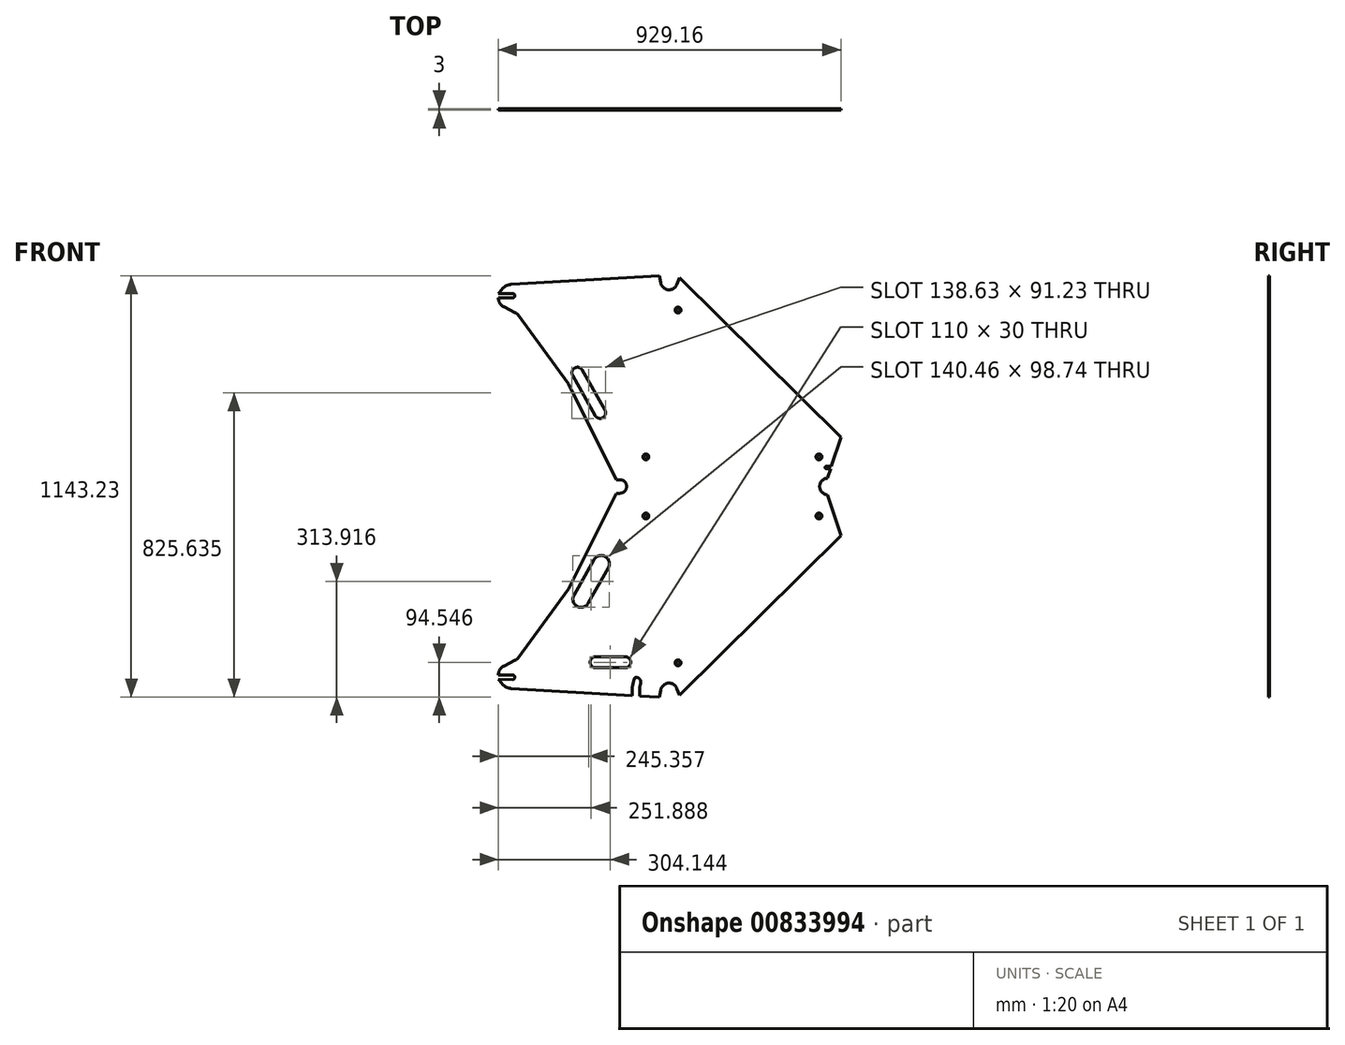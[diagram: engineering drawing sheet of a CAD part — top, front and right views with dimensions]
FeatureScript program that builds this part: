
annotation { "Feature Type Name" : "Feature", "Feature Type Description" : "" }
export const myFeature = defineFeature(function(context is Context, id is Id, definition is map)
    precondition{}
    {
        {
            var Q0;
            Q0=qCreatedBy(makeId("Front.planeOp"),FACE);
            var sketch = newSketch(context, id + "F0", { "sketchPlane" : qUnion([Q0])});
            skLineSegment(sketch, "E0", {"start": v(-160.76, 555.88) * mm, "end": v(408.24, 555.88) * mm, "construction": true});
            skLineSegment(sketch, "E1", {"start": v(408.24, 555.88) * mm, "end": v(445.83, 440.87) * mm, "construction": true});
            skArc(sketch, "E2", {"start": v(0.74, 26.27) * mm, "mid": v(-22.4, 40.64) * mm, "end": v(-42.43, 22.2) * mm});
            skLineSegment(sketch, "E3", {"start": v(-20.28, 18.24) * mm, "end": v(-144.86, 555.88) * mm, "construction": true});
            skLineSegment(sketch, "E4", {"start": v(-160.76, 555.88) * mm, "end": v(-39.05, 30.64) * mm, "construction": true});
            skLineSegment(sketch, "E5", {"start": v(-128.12, 555.88) * mm, "end": v(-7.89, 37.02) * mm, "construction": true});
            skLineSegment(sketch, "E6", {"start": v(0, 0) * mm, "end": v(-484.19, 28.1) * mm, "construction": true});
            skLineSegment(sketch, "E7", {"start": v(-160.76, 555.88) * mm, "end": v(-484.19, 28.1) * mm, "construction": true});
            skLineSegment(sketch, "E8", {"start": v(445.83, 440.87) * mm, "end": v(0, 0) * mm, "construction": true});
            skPoint(sketch, "E9", {"position": v(-176.43, 530.3) * mm});
            skPoint(sketch, "E10", {"position": v(-312.28, 308.61) * mm});
            skLineSegment(sketch, "E11", {"start": v(-312.28, 308.61) * mm, "end": v(-292.67, 296.6) * mm, "construction": true});
            skLineSegment(sketch, "E12", {"start": v(-176.43, 530.3) * mm, "end": v(-292.67, 296.6) * mm});
            skLineSegment(sketch, "E13", {"start": v(-429.8, 108.64) * mm, "end": v(-292.67, 296.6) * mm});
            skLineSegment(sketch, "E14", {"start": v(397.8, 555.88) * mm, "end": v(-163.71, 555.88) * mm});
            skLineSegment(sketch, "E15", {"start": v(409.57, 551.8) * mm, "end": v(445.83, 440.87) * mm});
            skLineSegment(sketch, "E16", {"start": v(445.83, 440.87) * mm, "end": v(7.82, 7.73) * mm});
            skPoint(sketch, "E17", {"position": v(-45.92, 2.66) * mm});
            skPoint(sketch, "E18", {"position": v(7.82, 7.73) * mm});
            skArc(sketch, "E19", {"start": v(7.82, 7.73) * mm, "mid": v(-23.1, 48.1) * mm, "end": v(-45.92, 2.66) * mm, "construction": true});
            skLineSegment(sketch, "E20", {"start": v(-176.43, 530.3) * mm, "end": v(-163.71, 555.88) * mm});
            skLineSegment(sketch, "E21", {"start": v(-173.75, 373) * mm, "end": v(-249.95, 238.03) * mm, "construction": true});
            skLineSegment(sketch, "E22", {"start": v(-186.81, 380.38) * mm, "end": v(-263, 245.4) * mm, "construction": true});
            skPoint(sketch, "E23.visualSharp", {"position": v(-289.13, 260.15) * mm});
            skPoint(sketch, "E24.visualSharp", {"position": v(-249.95, 238.03) * mm});
            skLineSegment(sketch, "E25", {"start": v(-212.94, 395.13) * mm, "end": v(-289.13, 260.15) * mm, "construction": true});
            skLineSegment(sketch, "E26", {"start": v(-249.95, 238.03) * mm, "end": v(-289.13, 260.15) * mm, "construction": true});
            skLineSegment(sketch, "E27", {"start": v(-212.94, 395.13) * mm, "end": v(-173.75, 373) * mm, "construction": true});
            skLineSegment(sketch, "E28", {"start": v(-292.67, 296.6) * mm, "end": v(-274.39, 286.27) * mm, "construction": true});
            skArc(sketch, "E29", {"start": v(-278.07, 279.74) * mm, "mid": v(-269.54, 249.09) * mm, "end": v(-238.88, 257.62) * mm});
            skLineSegment(sketch, "E30", {"start": v(-278.07, 279.74) * mm, "end": v(-238.88, 257.62) * mm, "construction": true});
            skArc(sketch, "E31", {"start": v(-184.81, 353.41) * mm, "mid": v(-193.34, 384.07) * mm, "end": v(-224, 375.53) * mm});
            skLineSegment(sketch, "E32", {"start": v(-224, 375.53) * mm, "end": v(-184.81, 353.41) * mm, "construction": true});
            skLineSegment(sketch, "E33", {"start": v(-278.07, 279.74) * mm, "end": v(-224, 375.53) * mm});
            skLineSegment(sketch, "E34", {"start": v(-184.81, 353.41) * mm, "end": v(-238.88, 257.62) * mm});
            skLineSegment(sketch, "E35.bottom", {"start": v(-234.19, 112.2) * mm, "end": v(-124.19, 112.2) * mm, "construction": true});
            skLineSegment(sketch, "E35.top", {"start": v(-234.19, 82.2) * mm, "end": v(-124.19, 82.2) * mm, "construction": true});
            skLineSegment(sketch, "E35.left", {"start": v(-234.19, 112.2) * mm, "end": v(-234.19, 82.2) * mm, "construction": true});
            skLineSegment(sketch, "E35.right", {"start": v(-124.19, 112.2) * mm, "end": v(-124.19, 82.2) * mm, "construction": true});
            skLineSegment(sketch, "E36", {"start": v(-124.19, 82.2) * mm, "end": v(-124.19, 7.2) * mm, "construction": true});
            skArc(sketch, "E37", {"start": v(-219.19, 112.2) * mm, "mid": v(-234.19, 97.2) * mm, "end": v(-219.19, 82.2) * mm});
            skArc(sketch, "E38", {"start": v(-139.19, 82.2) * mm, "mid": v(-124.19, 97.2) * mm, "end": v(-139.19, 112.2) * mm});
            skLineSegment(sketch, "E39", {"start": v(-139.19, 112.2) * mm, "end": v(-139.19, 82.2) * mm, "construction": true});
            skLineSegment(sketch, "E40", {"start": v(-219.19, 112.2) * mm, "end": v(-139.19, 112.2) * mm});
            skLineSegment(sketch, "E41", {"start": v(-139.19, 82.2) * mm, "end": v(-219.19, 82.2) * mm});
            skLineSegment(sketch, "E42", {"start": v(-641.86, 574.28) * mm, "end": v(862.04, 574.28) * mm, "construction": true});
            skLineSegment(sketch, "E43.MirrorCS", {"start": v(-312.28, 839.94) * mm, "end": v(-292.67, 851.96) * mm, "construction": true});
            skLineSegment(sketch, "E44.MirrorCS", {"start": v(-176.43, 618.26) * mm, "end": v(-163.71, 592.68) * mm});
            skLineSegment(sketch, "E45.MirrorCS", {"start": v(-249.95, 910.53) * mm, "end": v(-289.13, 888.41) * mm, "construction": true});
            skLineSegment(sketch, "E46.MirrorCS", {"start": v(-447.54, 1122.59) * mm, "end": v(-461.2, 1082.95) * mm, "construction": true});
            skLineSegment(sketch, "E47.MirrorCS", {"start": v(-212.94, 753.43) * mm, "end": v(-173.75, 775.55) * mm, "construction": true});
            skLineSegment(sketch, "E48.MirrorCS", {"start": v(-292.67, 851.96) * mm, "end": v(-274.39, 862.29) * mm, "construction": true});
            skLineSegment(sketch, "E49.MirrorCS", {"start": v(-45.92, 1145.9) * mm, "end": v(-447.54, 1122.59) * mm});
            skArc(sketch, "E50.MirrorC", {"start": v(0.74, 1122.29) * mm, "mid": v(-22.4, 1107.92) * mm, "end": v(-42.43, 1126.36) * mm});
            skLineSegment(sketch, "E51.MirrorCS", {"start": v(445.83, 707.7) * mm, "end": v(7.82, 1140.82) * mm});
            skLineSegment(sketch, "E52.MirrorCS", {"start": v(397.8, 592.68) * mm, "end": v(-163.71, 592.68) * mm});
            skLineSegment(sketch, "E53.MirrorCS", {"start": v(409.57, 596.75) * mm, "end": v(418.05, 622.68) * mm});
            skArc(sketch, "E54.MirrorCS", {"start": v(7.82, 1140.82) * mm, "mid": v(-23.1, 1100.45) * mm, "end": v(-45.92, 1145.9) * mm, "construction": true});
            skPoint(sketch, "E55.MirrorP", {"position": v(-289.13, 888.41) * mm});
            skLineSegment(sketch, "E56.MirrorCS", {"start": v(-20.28, 1130.32) * mm, "end": v(-144.86, 592.68) * mm, "construction": true});
            skPoint(sketch, "E57.MirrorP", {"position": v(-312.28, 839.94) * mm});
            skLineSegment(sketch, "E58.MirrorCS", {"start": v(-128.12, 592.68) * mm, "end": v(-7.89, 1111.54) * mm, "construction": true});
            skPoint(sketch, "E59.MirrorP", {"position": v(-176.43, 618.26) * mm});
            skPoint(sketch, "E60.MirrorP", {"position": v(-45.92, 1145.9) * mm});
            skLineSegment(sketch, "E61.MirrorCS", {"start": v(-160.76, 592.68) * mm, "end": v(397.8, 592.68) * mm, "construction": true});
            skPoint(sketch, "E62.MirrorP", {"position": v(7.82, 1140.82) * mm});
            skLineSegment(sketch, "E63.MirrorCS", {"start": v(-160.76, 592.68) * mm, "end": v(-39.05, 1117.92) * mm, "construction": true});
            skLineSegment(sketch, "E64.MirrorCS", {"start": v(-160.76, 592.68) * mm, "end": v(-484.19, 1120.46) * mm, "construction": true});
            skLineSegment(sketch, "E65.MirrorCS", {"start": v(-186.81, 768.18) * mm, "end": v(-263, 903.16) * mm, "construction": true});
            skPoint(sketch, "E66.MirrorP", {"position": v(-249.95, 910.53) * mm});
            skPoint(sketch, "E67.MirrorP", {"position": v(-461.2, 1082.95) * mm});
            skLineSegment(sketch, "E68.MirrorCS", {"start": v(445.83, 707.7) * mm, "end": v(0, 1148.56) * mm, "construction": true});
            skLineSegment(sketch, "E69.MirrorCS", {"start": v(409.57, 596.75) * mm, "end": v(418.05, 622.68) * mm, "construction": true});
            skLineSegment(sketch, "E70.MirrorCS", {"start": v(-461.2, 1082.95) * mm, "end": v(-292.67, 851.96) * mm});
            skLineSegment(sketch, "E71.MirrorCS", {"start": v(-176.43, 618.26) * mm, "end": v(-178.63, 622.68) * mm});
            skLineSegment(sketch, "E72.MirrorCS", {"start": v(0, 1148.56) * mm, "end": v(-484.19, 1120.46) * mm, "construction": true});
            skLineSegment(sketch, "E73", {"start": v(-255.63, 890.1) * mm, "end": v(-194.19, 781.24) * mm});
            skArc(sketch, "E74", {"start": v(-255.63, 890.1) * mm, "mid": v(-276.07, 895.78) * mm, "end": v(-281.76, 875.35) * mm});
            skLineSegment(sketch, "E75", {"start": v(-289.13, 888.41) * mm, "end": v(-212.94, 753.43) * mm, "construction": true});
            skLineSegment(sketch, "E76", {"start": v(-281.76, 875.35) * mm, "end": v(-255.63, 890.1) * mm, "construction": true});
            skArc(sketch, "E77", {"start": v(-220.31, 766.5) * mm, "mid": v(-199.88, 760.8) * mm, "end": v(-194.19, 781.24) * mm});
            skLineSegment(sketch, "E78", {"start": v(-220.31, 766.5) * mm, "end": v(-194.19, 781.24) * mm, "construction": true});
            skLineSegment(sketch, "E79", {"start": v(-281.76, 875.35) * mm, "end": v(-220.31, 766.5) * mm});
            skArc(sketch, "E80.trimOffspring", {"start": v(-153.71, 555.88) * mm, "mid": v(-135.31, 574.28) * mm, "end": v(-153.71, 592.68) * mm});
            skArc(sketch, "E81", {"start": v(409.57, 596.75) * mm, "mid": v(388.24, 574.28) * mm, "end": v(409.57, 551.8) * mm});
            skLineSegment(sketch, "E82", {"start": v(388.24, 592.68) * mm, "end": v(388.24, 555.88) * mm, "construction": true});
            skPoint(sketch, "E83.orphan", {"position": v(408.24, 592.68) * mm});
            skPoint(sketch, "E84.orphan", {"position": v(408.24, 555.88) * mm});
            skLineSegment(sketch, "E85", {"start": v(-437.04, 102.52) * mm, "end": v(-516.22, 63.05) * mm, "construction": true});
            skLineSegment(sketch, "E86", {"start": v(-516.22, 63.05) * mm, "end": v(-444.22, 62.36) * mm, "construction": true});
            skLineSegment(sketch, "E87", {"start": v(-438.28, 56.3) * mm, "end": v(-438.28, 56.3) * mm});
            skLineSegment(sketch, "E88", {"start": v(-444.33, 50.36) * mm, "end": v(-483.33, 50.74) * mm});
            skLineSegment(sketch, "E89", {"start": v(-483.33, 50.74) * mm, "end": v(-463.52, 26.9) * mm});
            skPoint(sketch, "E90.orphan", {"position": v(-439.25, 101.42) * mm});
            skPoint(sketch, "E91.end.orphan", {"position": v(-461.2, 65.61) * mm});
            skArc(sketch, "E92", {"start": v(-467.98, 87.1) * mm, "mid": v(-479.03, 77.06) * mm, "end": v(-483.22, 62.74) * mm});
            skLineSegment(sketch, "E93", {"start": v(-483.22, 62.74) * mm, "end": v(-482.71, 115.9) * mm, "construction": true});
            skPoint(sketch, "E94.visualSharp", {"position": v(-438.22, 62.3) * mm});
            skArc(sketch, "E94.filletArc", {"start": v(-438.28, 56.3) * mm, "mid": v(-440, 60.57) * mm, "end": v(-444.22, 62.36) * mm});
            skPoint(sketch, "E95.visualSharp", {"position": v(-438.33, 50.3) * mm});
            skArc(sketch, "E95.filletArc", {"start": v(-444.33, 50.36) * mm, "mid": v(-440.07, 52.08) * mm, "end": v(-438.28, 56.3) * mm});
            skLineSegment(sketch, "E96", {"start": v(-467.98, 87.1) * mm, "end": v(-437.04, 102.52) * mm, "construction": true});
            skLineSegment(sketch, "E97", {"start": v(-467.98, 87.1) * mm, "end": v(-437.04, 102.52) * mm});
            skLineSegment(sketch, "E98", {"start": v(-483.22, 62.74) * mm, "end": v(-444.22, 62.36) * mm});
            skLineSegment(sketch, "E99", {"start": v(-463.52, 26.9) * mm, "end": v(-447.54, 25.97) * mm, "construction": true});
            skArc(sketch, "E100", {"start": v(-473.74, 39.2) * mm, "mid": v(-462.02, 29.86) * mm, "end": v(-447.54, 25.97) * mm});
            skLineSegment(sketch, "E101", {"start": v(-483.22, 62.74) * mm, "end": v(-483.33, 50.74) * mm, "construction": true});
            skPoint(sketch, "E102.visualSharp", {"position": v(-432.68, 104.7) * mm});
            skArc(sketch, "E102.filletArc", {"start": v(-437.04, 102.52) * mm, "mid": v(-433.06, 105.15) * mm, "end": v(-429.8, 108.64) * mm});
            skLineSegment(sketch, "E103.MirrorCS", {"start": v(-467.98, 1061.46) * mm, "end": v(-437.04, 1046.03) * mm});
            skLineSegment(sketch, "E104.MirrorCS", {"start": v(-483.22, 1085.82) * mm, "end": v(-444.22, 1086.2) * mm});
            skArc(sketch, "E105.MirrorCS", {"start": v(-444.33, 1098.2) * mm, "mid": v(-440.07, 1096.48) * mm, "end": v(-438.28, 1092.25) * mm});
            skArc(sketch, "E106.MirrorCS", {"start": v(-438.28, 1092.25) * mm, "mid": v(-440, 1088) * mm, "end": v(-444.22, 1086.2) * mm});
            skArc(sketch, "E107.MirrorCS", {"start": v(-437.04, 1046.03) * mm, "mid": v(-433.06, 1043.41) * mm, "end": v(-429.8, 1039.92) * mm});
            skLineSegment(sketch, "E108.MirrorCS", {"start": v(-444.33, 1098.2) * mm, "end": v(-483.33, 1097.82) * mm});
            skLineSegment(sketch, "E109.MirrorCS", {"start": v(-463.52, 1121.66) * mm, "end": v(-447.54, 1122.59) * mm, "construction": true});
            skPoint(sketch, "E110.MirrorP", {"position": v(-438.22, 1086.25) * mm});
            skArc(sketch, "E111.MirrorCS", {"start": v(-473.74, 1109.36) * mm, "mid": v(-462.02, 1118.7) * mm, "end": v(-447.54, 1122.59) * mm});
            skLineSegment(sketch, "E112.MirrorCS", {"start": v(-516.22, 1085.5) * mm, "end": v(-444.22, 1086.2) * mm, "construction": true});
            skLineSegment(sketch, "E113.MirrorCS", {"start": v(-483.22, 1085.82) * mm, "end": v(-482.71, 1032.66) * mm, "construction": true});
            skArc(sketch, "E114.MirrorCS", {"start": v(-467.98, 1061.46) * mm, "mid": v(-479.03, 1071.5) * mm, "end": v(-483.22, 1085.82) * mm});
            skLineSegment(sketch, "E115.MirrorCS", {"start": v(-483.33, 1097.82) * mm, "end": v(-463.52, 1121.66) * mm});
            skPoint(sketch, "E116.MirrorP", {"position": v(-432.68, 1043.86) * mm});
            skPoint(sketch, "E117.MirrorP", {"position": v(-438.33, 1098.25) * mm});
            skLineSegment(sketch, "E118.MirrorCS", {"start": v(-467.98, 1061.46) * mm, "end": v(-437.04, 1046.03) * mm, "construction": true});
            skLineSegment(sketch, "E119.MirrorCS", {"start": v(-437.04, 1046.03) * mm, "end": v(-516.22, 1085.5) * mm, "construction": true});
            skLineSegment(sketch, "E120.MirrorCS", {"start": v(-483.22, 1085.82) * mm, "end": v(-483.33, 1097.82) * mm, "construction": true});
            skPoint(sketch, "E121.MirrorP", {"position": v(-439.25, 1047.14) * mm});
            skLineSegment(sketch, "E122", {"start": v(-91.14, 55.37) * mm, "end": v(-109, 56.4) * mm});
            skCircle(sketch, "E123", {"center": v(-20.28, 18.24) * mm, "radius": 100 * mm, "construction": true});
            skCircle(sketch, "E124", {"center": v(-20.28, 18.24) * mm, "radius": 80 * mm, "construction": true});
            skArc(sketch, "E125", {"start": v(-113.98, 53.16) * mm, "mid": v(-119.54, 30.39) * mm, "end": v(-119.64, 6.94) * mm});
            skArc(sketch, "E126", {"start": v(-91.14, 55.37) * mm, "mid": v(-99.22, 31.23) * mm, "end": v(-99.3, 5.76) * mm});
            skPoint(sketch, "E127.visualSharp", {"position": v(-112.62, 56.62) * mm});
            skArc(sketch, "E127.filletArc", {"start": v(-109, 56.4) * mm, "mid": v(-112.03, 55.6) * mm, "end": v(-113.98, 53.16) * mm});
            skLineSegment(sketch, "E128", {"start": v(-119.64, 6.94) * mm, "end": v(-447.54, 25.97) * mm});
            skLineSegment(sketch, "E129", {"start": v(-99.3, 5.76) * mm, "end": v(-45.92, 2.66) * mm});
            skLineSegment(sketch, "E130", {"start": v(-120.75, 624.48) * mm, "end": v(418.63, 624.48) * mm, "construction": true});
            skLineSegment(sketch, "E131", {"start": v(437.88, 715.55) * mm, "end": v(397.7, 592.61) * mm, "construction": true});
            skLineSegment(sketch, "E132", {"start": v(0, 1108.22) * mm, "end": v(435.87, 677.2) * mm, "construction": true});
            skLineSegment(sketch, "E133", {"start": v(-153.71, 592.68) * mm, "end": v(-153.71, 555.88) * mm, "construction": true});
            skLineSegment(sketch, "E134", {"start": v(-42.43, 22.2) * mm, "end": v(-45.92, 2.66) * mm});
            skLineSegment(sketch, "E135", {"start": v(0.74, 26.27) * mm, "end": v(7.82, 7.73) * mm});
            skLineSegment(sketch, "E136", {"start": v(-45.92, 1145.9) * mm, "end": v(-42.43, 1126.36) * mm});
            skLineSegment(sketch, "E137", {"start": v(0.74, 1122.29) * mm, "end": v(7.82, 1140.82) * mm});
            skArc(sketch, "E138", {"start": v(-97.28, 39.95) * mm, "mid": v(-99.2, 50.99) * mm, "end": v(-109, 56.4) * mm});
            skLineSegment(sketch, "E139", {"start": v(-530.7, 62.82) * mm, "end": v(-438.1, 61.94) * mm, "construction": true});
            skLineSegment(sketch, "E140", {"start": v(-438.1, 61.94) * mm, "end": v(-438.2, 50.97) * mm, "construction": true});
            skLineSegment(sketch, "E141", {"start": v(-438.2, 50.97) * mm, "end": v(-529.63, 51.84) * mm, "construction": true});
            skLineSegment(sketch, "E142.trimOffspring", {"start": v(-178.63, 622.68) * mm, "end": v(-292.67, 851.96) * mm});
            skLineSegment(sketch, "E143", {"start": v(431.28, 622.68) * mm, "end": v(406.05, 622.68) * mm, "construction": true});
            skLineSegment(sketch, "E144", {"start": v(418.05, 622.68) * mm, "end": v(403.05, 622.68) * mm});
            skLineSegment(sketch, "E145", {"start": v(403.05, 625.68) * mm, "end": v(403.05, 625.68) * mm});
            skLineSegment(sketch, "E146", {"start": v(406.05, 628.68) * mm, "end": v(420, 628.68) * mm});
            skPoint(sketch, "E147.visualSharp", {"position": v(403.05, 628.68) * mm});
            skArc(sketch, "E147.filletArc", {"start": v(406.05, 628.68) * mm, "mid": v(403.92, 627.8) * mm, "end": v(403.05, 625.68) * mm});
            skPoint(sketch, "E148.newPointA", {"position": v(403.05, 622.68) * mm});
            skArc(sketch, "E148.filletArc", {"start": v(403.05, 625.68) * mm, "mid": v(403.92, 623.56) * mm, "end": v(406.05, 622.68) * mm});
            skLineSegment(sketch, "E149.trimOffspring", {"start": v(420, 628.68) * mm, "end": v(445.83, 707.7) * mm, "construction": true});
            skLineSegment(sketch, "E150.trimOffspring", {"start": v(420, 628.68) * mm, "end": v(445.83, 707.7) * mm});
            skPoint(sketch, "E151", {"position": v(-83, 654.48) * mm});
            skPoint(sketch, "E152", {"position": v(4.2, 1052.99) * mm});
            skPoint(sketch, "E153", {"position": v(386.36, 654.48) * mm});
            skPoint(sketch, "E154.MirrorP", {"position": v(386.36, 494.08) * mm});
            skPoint(sketch, "E155.MirrorP", {"position": v(-83, 494.08) * mm});
            skPoint(sketch, "E156.MirrorP", {"position": v(4.2, 95.57) * mm});
            skSolve(sketch);
        }
        {
            var Q0;
            Q0=qSketchRegion(id+"F0",true);
            extrude(context, id + "F1", {"entities" : qUnion([Q0]), "oppositeDirection" : true, "depth" : 3 * mm, "offsetDistance" : 25 * mm});
        }
        {
            var Q0;
            Q0=sQuery(id+"F0.wireOp",VERTEX,"E154.MirrorP");
            var Q1;
            Q1=sQuery(id+"F0.wireOp",VERTEX,"E155.MirrorP");
            var Q2;
            Q2=sQuery(id+"F0.wireOp",VERTEX,"E156.MirrorP");
            var Q3;
            Q3=sQuery(id+"F0.wireOp",VERTEX,"E151");
            var Q4;
            Q4=sQuery(id+"F0.wireOp",VERTEX,"E152");
            var Q5;
            Q5=sQuery(id+"F0.wireOp",VERTEX,"E153");
            var Q6;
            Q6=makeQuery(id+"F1.opExtrude","SWEPT_BODY",BODY,{"disambiguationData":[OSD([sQuery(id+"F0.wireOp",EDGE,"E2"),sQuery(id+"F0.wireOp",EDGE,"E12"),sQuery(id+"F0.wireOp",EDGE,"E13"),sQuery(id+"F0.wireOp",EDGE,"E14"),sQuery(id+"F0.wireOp",EDGE,"E15"),sQuery(id+"F0.wireOp",EDGE,"E16"),sQuery(id+"F0.wireOp",EDGE,"E20"),sQuery(id+"F0.wireOp",EDGE,"E29"),sQuery(id+"F0.wireOp",EDGE,"E31"),sQuery(id+"F0.wireOp",EDGE,"E33"),sQuery(id+"F0.wireOp",EDGE,"E34"),sQuery(id+"F0.wireOp",EDGE,"E37"),sQuery(id+"F0.wireOp",EDGE,"E38"),sQuery(id+"F0.wireOp",EDGE,"E40"),sQuery(id+"F0.wireOp",EDGE,"E41"),sQuery(id+"F0.wireOp",EDGE,"E44.MirrorCS"),sQuery(id+"F0.wireOp",EDGE,"E49.MirrorCS"),sQuery(id+"F0.wireOp",EDGE,"E50.MirrorC"),sQuery(id+"F0.wireOp",EDGE,"E51.MirrorCS"),sQuery(id+"F0.wireOp",EDGE,"E52.MirrorCS"),sQuery(id+"F0.wireOp",EDGE,"E53.MirrorCS"),sQuery(id+"F0.wireOp",EDGE,"E70.MirrorCS"),sQuery(id+"F0.wireOp",EDGE,"E71.MirrorCS"),sQuery(id+"F0.wireOp",EDGE,"E73"),sQuery(id+"F0.wireOp",EDGE,"E74"),sQuery(id+"F0.wireOp",EDGE,"E77"),sQuery(id+"F0.wireOp",EDGE,"E79"),sQuery(id+"F0.wireOp",EDGE,"E80.trimOffspring"),sQuery(id+"F0.wireOp",EDGE,"E81"),sQuery(id+"F0.wireOp",EDGE,"E88"),sQuery(id+"F0.wireOp",EDGE,"E89"),sQuery(id+"F0.wireOp",EDGE,"E92"),sQuery(id+"F0.wireOp",EDGE,"E94.filletArc"),sQuery(id+"F0.wireOp",EDGE,"E95.filletArc"),sQuery(id+"F0.wireOp",EDGE,"E97"),sQuery(id+"F0.wireOp",EDGE,"E98"),sQuery(id+"F0.wireOp",EDGE,"E100"),sQuery(id+"F0.wireOp",EDGE,"E102.filletArc"),sQuery(id+"F0.wireOp",EDGE,"E103.MirrorCS"),sQuery(id+"F0.wireOp",EDGE,"E104.MirrorCS"),sQuery(id+"F0.wireOp",EDGE,"E105.MirrorCS"),sQuery(id+"F0.wireOp",EDGE,"E106.MirrorCS"),sQuery(id+"F0.wireOp",EDGE,"E107.MirrorCS"),sQuery(id+"F0.wireOp",EDGE,"E108.MirrorCS"),sQuery(id+"F0.wireOp",EDGE,"E111.MirrorCS"),sQuery(id+"F0.wireOp",EDGE,"E114.MirrorCS"),sQuery(id+"F0.wireOp",EDGE,"E115.MirrorCS"),sQuery(id+"F0.wireOp",EDGE,"E125"),sQuery(id+"F0.wireOp",EDGE,"E126"),sQuery(id+"F0.wireOp",EDGE,"E127.filletArc"),sQuery(id+"F0.wireOp",EDGE,"E128"),sQuery(id+"F0.wireOp",EDGE,"E129"),sQuery(id+"F0.wireOp",EDGE,"E134"),sQuery(id+"F0.wireOp",EDGE,"E135"),sQuery(id+"F0.wireOp",EDGE,"E136"),sQuery(id+"F0.wireOp",EDGE,"E137"),sQuery(id+"F0.wireOp",EDGE,"E138"),sQuery(id+"F0.wireOp",EDGE,"E142.trimOffspring"),sQuery(id+"F0.wireOp",EDGE,"E144"),sQuery(id+"F0.wireOp",EDGE,"E146"),sQuery(id+"F0.wireOp",EDGE,"E147.filletArc"),sQuery(id+"F0.wireOp",EDGE,"E148.filletArc"),sQuery(id+"F0.wireOp",EDGE,"E150.trimOffspring")])]});
            hole(context, id + "F2", {"style" : HoleStyle.C_SINK, "endStyle" : HoleEndStyle.THROUGH, "holeDiameter" : 8 * mm, "cSinkDiameter" : 16 * mm, "cSinkAngle" : 90 * degree, "majorDiameter" : 5 * mm, "isTappedThrough" : true, "tappedDepth" : 12 * mm, "tapClearance" : 3, "locations" : qUnion([Q0, Q1, Q2, Q3, Q4, Q5]), "scope" : qUnion([Q6])});
        }
    });
